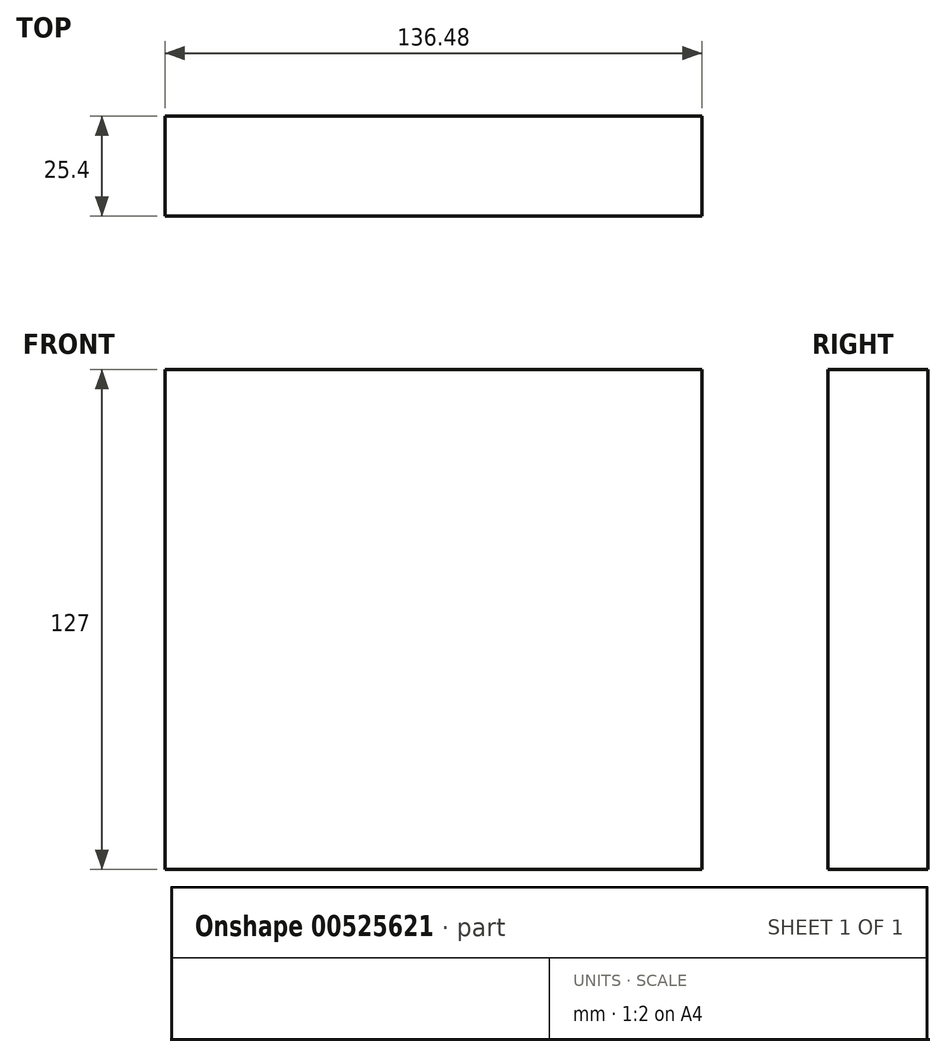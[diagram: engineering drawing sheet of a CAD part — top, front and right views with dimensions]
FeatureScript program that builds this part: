
annotation { "Feature Type Name" : "Feature", "Feature Type Description" : "" }
export const myFeature = defineFeature(function(context is Context, id is Id, definition is map)
    precondition{}
    {
        {
            var Q0;
            Q0=qCreatedBy(makeId("Front.planeOp"),FACE);
            var sketch = newSketch(context, id + "F0", { "sketchPlane" : qUnion([Q0])});
            skLineSegment(sketch, "E0.bottom", {"start": v(-21.98, -37.78) * mm, "end": v(114.5, -37.78) * mm});
            skLineSegment(sketch, "E0.top", {"start": v(-21.98, 123.46) * mm, "end": v(114.5, 123.46) * mm});
            skLineSegment(sketch, "E0.left", {"start": v(-21.98, -37.78) * mm, "end": v(-21.98, 123.46) * mm});
            skLineSegment(sketch, "E0.right", {"start": v(114.5, -37.78) * mm, "end": v(114.5, 123.46) * mm});
            skPoint(sketch, "E0.middle", {"position": v(46.26, 42.84) * mm});
            skLineSegment(sketch, "E1.bottom", {"start": v(0, 16.13) * mm, "end": v(30, 16.13) * mm});
            skLineSegment(sketch, "E1.top", {"start": v(0, 43.1) * mm, "end": v(30, 43.1) * mm});
            skLineSegment(sketch, "E1.left", {"start": v(0, 16.13) * mm, "end": v(0, 43.1) * mm});
            skLineSegment(sketch, "E1.right", {"start": v(30, 16.13) * mm, "end": v(30, 43.1) * mm});
            skPoint(sketch, "E1.middle", {"position": v(15, 29.61) * mm});
            skSolve(sketch);
        }
        {
            var Q0;
            Q0 = qSketchRegion(id + "F0", true);
            var Q1;
            Q1=sQuery(id+"F0.wireOp",EDGE,"E0.bottom");
            extrude(context, id + "F1", {"entities" : qUnion([Q0]), "bodyType" : ToolBodyType.SURFACE, "surfaceEntities" : qUnion([Q1]), "depth" : 25.4 * mm, "offsetDistance" : 25.4 * mm});
        }
        {
            var Q0;
            Q0=makeQuery(id+"F1.opExtrude","SWEPT_FACE",FACE,{"disambiguationData":[OSD([sQuery(id+"F0.wireOp",EDGE,"E0.bottom")])]});
            extrude(context, id + "F2", {"entities" : qUnion([Q0]), "depth" : 127 * mm, "offsetDistance" : 25.4 * mm});
        }
    });
